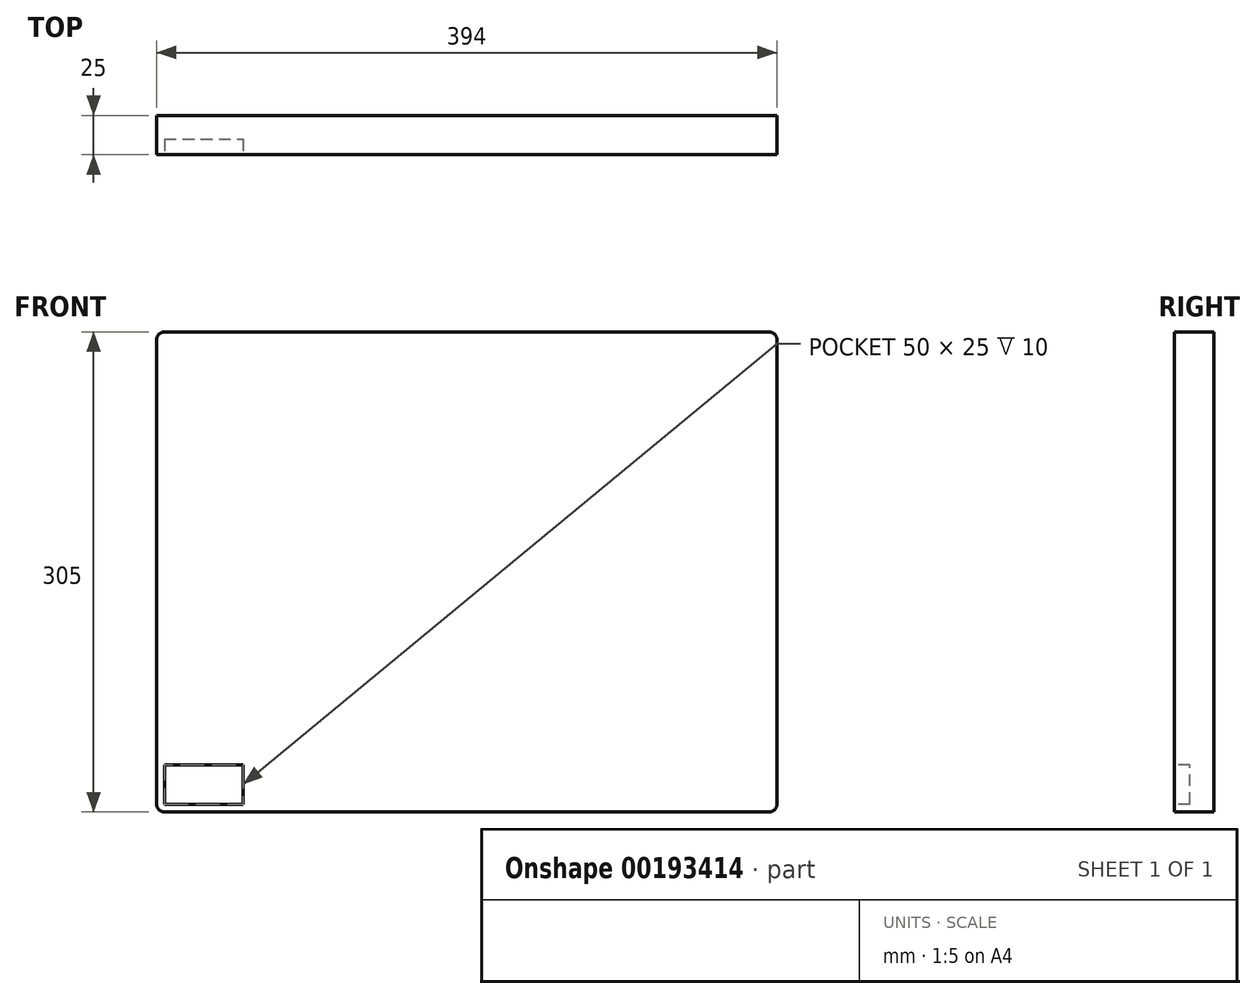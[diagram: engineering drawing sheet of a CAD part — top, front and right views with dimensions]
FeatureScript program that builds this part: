
annotation { "Feature Type Name" : "Feature", "Feature Type Description" : "" }
export const myFeature = defineFeature(function(context is Context, id is Id, definition is map)
    precondition{}
    {
        {
            var Q0;
            Q0=qCreatedBy(makeId("Front.planeOp"),FACE);
            var sketch = newSketch(context, id + "F0", { "sketchPlane" : qUnion([Q0])});
            skLineSegment(sketch, "E0.bottom", {"start": v(5, 0) * mm, "end": v(389, 0) * mm});
            skLineSegment(sketch, "E0.top", {"start": v(5, 305) * mm, "end": v(389, 305) * mm});
            skLineSegment(sketch, "E0.left", {"start": v(0, 5) * mm, "end": v(0, 300) * mm});
            skLineSegment(sketch, "E0.right", {"start": v(394, 5) * mm, "end": v(394, 300) * mm});
            skPoint(sketch, "E1.visualSharp", {"position": v(0, 0) * mm});
            skArc(sketch, "E1.filletArc", {"start": v(0, 5) * mm, "mid": v(1.46, 1.46) * mm, "end": v(5, 0) * mm});
            skPoint(sketch, "E2.visualSharp", {"position": v(394, 0) * mm});
            skArc(sketch, "E2.filletArc", {"start": v(389, 0) * mm, "mid": v(392.54, 1.46) * mm, "end": v(394, 5) * mm});
            skPoint(sketch, "E3.visualSharp", {"position": v(394, 305) * mm});
            skArc(sketch, "E3.filletArc", {"start": v(394, 300) * mm, "mid": v(392.54, 303.54) * mm, "end": v(389, 305) * mm});
            skPoint(sketch, "E4.visualSharp", {"position": v(0, 305) * mm});
            skArc(sketch, "E4.filletArc", {"start": v(5, 305) * mm, "mid": v(1.46, 303.54) * mm, "end": v(0, 300) * mm});
            skSolve(sketch);
        }
        {
            var Q0;
            Q0=makeQuery(id+"F0.imprint","IMPRINT",FACE,{"disambiguationData":[TD([[makeQuery(id+"F0.imprint","IMPRINT",EDGE,{"derivedFrom":sQuery(id+"F0.wireOp",EDGE,"E0.bottom")}),1.0]])]});
            extrude(context, id + "F1", {"entities" : qUnion([Q0]), "depth" : 25 * mm});
        }
        {
            var Q0;
            Q0=makeQuery(id+"F1.opExtrude","CAP_FACE",FACE,{"disambiguationData":[OSD([sQuery(id+"F0.wireOp",EDGE,"E0.bottom"),sQuery(id+"F0.wireOp",EDGE,"E0.top"),sQuery(id+"F0.wireOp",EDGE,"E0.left"),sQuery(id+"F0.wireOp",EDGE,"E0.right"),sQuery(id+"F0.wireOp",EDGE,"E1.filletArc"),sQuery(id+"F0.wireOp",EDGE,"E2.filletArc"),sQuery(id+"F0.wireOp",EDGE,"E3.filletArc"),sQuery(id+"F0.wireOp",EDGE,"E4.filletArc")])],"isStart":false});
            var sketch = newSketch(context, id + "F2", { "sketchPlane" : qUnion([Q0])});
            skLineSegment(sketch, "E5.bottom", {"start": v(5, 5) * mm, "end": v(55, 5) * mm});
            skLineSegment(sketch, "E5.top", {"start": v(5, 30) * mm, "end": v(55, 30) * mm});
            skLineSegment(sketch, "E5.left", {"start": v(5, 5) * mm, "end": v(5, 30) * mm});
            skLineSegment(sketch, "E5.right", {"start": v(55, 5) * mm, "end": v(55, 30) * mm});
            skSolve(sketch);
        }
        {
            var Q0;
            Q0=makeQuery(id+"F2.imprint","IMPRINT",FACE,{"disambiguationData":[TD([[makeQuery(id+"F2.imprint","IMPRINT",EDGE,{"derivedFrom":sQuery(id+"F2.wireOp",EDGE,"E5.bottom")}),1.0]])]});
            extrude(context, id + "F3", {"entities" : qUnion([Q0]), "operationType" : NewBodyOperationType.REMOVE, "oppositeDirection" : true, "depth" : 10 * mm});
        }
    });
